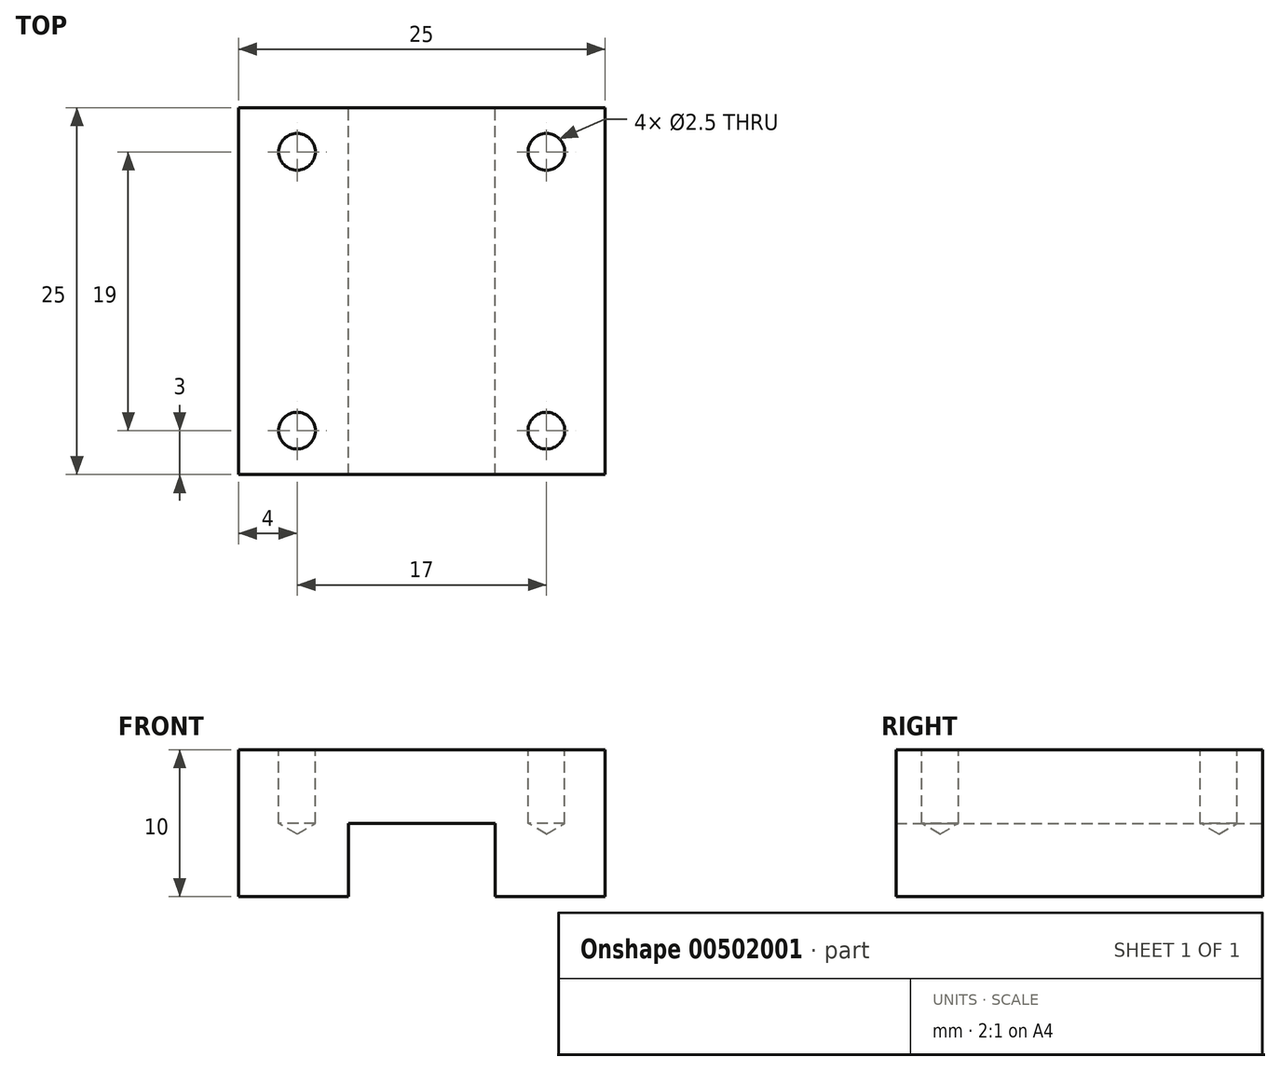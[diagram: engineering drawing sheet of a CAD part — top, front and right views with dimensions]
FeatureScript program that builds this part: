
annotation { "Feature Type Name" : "Feature", "Feature Type Description" : "" }
export const myFeature = defineFeature(function(context is Context, id is Id, definition is map)
    precondition{}
    {
        {
            var Q0;
            Q0=qCreatedBy(makeId("Front.planeOp"),FACE);
            var sketch = newSketch(context, id + "F0", { "sketchPlane" : qUnion([Q0])});
            skLineSegment(sketch, "E0", {"start": v(0, 0) * mm, "end": v(5, 0) * mm});
            skLineSegment(sketch, "E1", {"start": v(5, 0) * mm, "end": v(5, -5) * mm});
            skLineSegment(sketch, "E2", {"start": v(5, -5) * mm, "end": v(12.5, -5) * mm});
            skLineSegment(sketch, "E3", {"start": v(12.5, -5) * mm, "end": v(12.5, 5) * mm});
            skLineSegment(sketch, "E4", {"start": v(12.5, 5) * mm, "end": v(0, 5) * mm});
            skLineSegment(sketch, "E5", {"start": v(0, 5) * mm, "end": v(0, 0) * mm, "construction": true});
            skLineSegment(sketch, "E6.MirrorCS", {"start": v(-12.5, 5) * mm, "end": v(0, 5) * mm});
            skLineSegment(sketch, "E7.MirrorCS", {"start": v(0, 0) * mm, "end": v(-5, 0) * mm});
            skLineSegment(sketch, "E8.MirrorCS", {"start": v(-5, 0) * mm, "end": v(-5, -5) * mm});
            skLineSegment(sketch, "E9.MirrorCS", {"start": v(-5, -5) * mm, "end": v(-12.5, -5) * mm});
            skLineSegment(sketch, "E10.MirrorCS", {"start": v(-12.5, -5) * mm, "end": v(-12.5, 5) * mm});
            skSolve(sketch);
        }
        {
            var Q0;
            Q0 = qSketchRegion(id + "F0", true);
            extrude(context, id + "F1", {"entities" : qUnion([Q0]), "depth" : 25 * mm});
        }
        {
            var Q0;
            Q0=makeQuery(id+"F1.opExtrude","SWEPT_FACE",FACE,{"disambiguationData":[OSD([sQuery(id+"F0.wireOp",EDGE,"E4"),sQuery(id+"F0.wireOp",EDGE,"E6.MirrorCS")])]});
            var sketch = newSketch(context, id + "F2", { "sketchPlane" : qUnion([Q0])});
            skCircle(sketch, "E11", {"center": v(8.5, -3) * mm, "radius": 1.25 * mm});
            skLineSegment(sketch, "E12", {"start": v(-12.5, -12.5) * mm, "end": v(12.5, -12.5) * mm, "construction": true});
            skLineSegment(sketch, "E13", {"start": v(0, -25) * mm, "end": v(0, 0) * mm, "construction": true});
            skCircle(sketch, "E14.MirrorC", {"center": v(8.5, -22) * mm, "radius": 1.25 * mm});
            skCircle(sketch, "E15.MirrorC", {"center": v(-8.5, -3) * mm, "radius": 1.25 * mm});
            skCircle(sketch, "E16.MirrorC", {"center": v(-8.5, -22) * mm, "radius": 1.25 * mm});
            skSolve(sketch);
        }
        {
            var Q0;
            Q0=sQuery(id+"F2.wireOp",VERTEX,"E15.MirrorC.center");
            var Q1;
            Q1=sQuery(id+"F2.wireOp",VERTEX,"E11.center");
            var Q2;
            Q2=sQuery(id+"F2.wireOp",VERTEX,"E16.MirrorC.center");
            var Q3;
            Q3=sQuery(id+"F2.wireOp",VERTEX,"E14.MirrorC.center");
            var Q4;
            Q4=makeQuery(id+"F1.opExtrude","SWEPT_BODY",BODY,{"disambiguationData":[OSD([sQuery(id+"F0.wireOp",EDGE,"E0"),sQuery(id+"F0.wireOp",EDGE,"E1"),sQuery(id+"F0.wireOp",EDGE,"E2"),sQuery(id+"F0.wireOp",EDGE,"E3"),sQuery(id+"F0.wireOp",EDGE,"E4"),sQuery(id+"F0.wireOp",EDGE,"E6.MirrorCS"),sQuery(id+"F0.wireOp",EDGE,"E7.MirrorCS"),sQuery(id+"F0.wireOp",EDGE,"E8.MirrorCS"),sQuery(id+"F0.wireOp",EDGE,"E9.MirrorCS"),sQuery(id+"F0.wireOp",EDGE,"E10.MirrorCS")])]});
            hole(context, id + "F3", {"style" : HoleStyle.SIMPLE, "endStyle" : HoleEndStyle.BLIND, "holeDiameter" : 2.5 * mm, "holeDepth" : 5 * mm, "isTappedThrough" : true, "tappedDepth" : 12 * mm, "tapClearance" : 3, "startFromSketch" : true, "locations" : qUnion([Q0, Q1, Q2, Q3]), "scope" : qUnion([Q4])});
        }
    });
